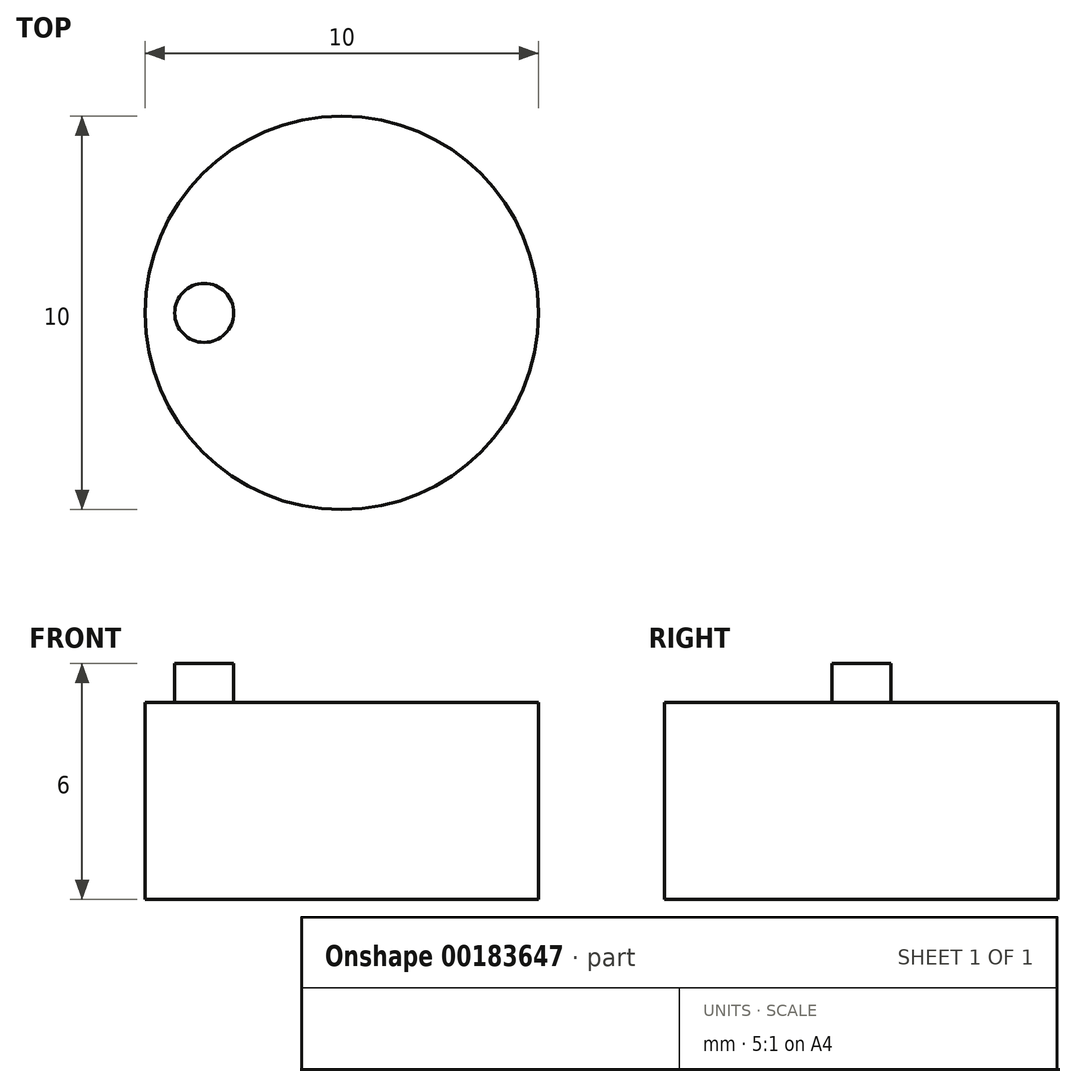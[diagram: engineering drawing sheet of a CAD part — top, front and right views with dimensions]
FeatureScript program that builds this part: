
annotation { "Feature Type Name" : "Feature", "Feature Type Description" : "" }
export const myFeature = defineFeature(function(context is Context, id is Id, definition is map)
    precondition{}
    {
        {
            var Q0;
            Q0=qCreatedBy(makeId("Top.planeOp"),FACE);
            var sketch = newSketch(context, id + "F0", { "sketchPlane" : qUnion([Q0])});
            skCircle(sketch, "E0", {"center": v(0, 0) * mm, "radius": 5 * mm});
            skLineSegment(sketch, "E1", {"start": v(-5, 0) * mm, "end": v(-3.5, 0) * mm});
            skPoint(sketch, "E2", {"position": v(-3.5, 0) * mm});
            skSolve(sketch);
        }
        {
            var Q0;
            Q0 = qSketchRegion(id + "F0", true);
            extrude(context, id + "F1", {"entities" : qUnion([Q0]), "depth" : 5 * mm});
        }
        {
            var Q0;
            Q0=makeQuery(id+"F1.opExtrude","CAP_FACE",FACE,{"disambiguationData":[OSD([sQuery(id+"F0.wireOp",EDGE,"E0")])],"isStart":false});
            var sketch = newSketch(context, id + "F2", { "sketchPlane" : qUnion([Q0])});
            skLineSegment(sketch, "E3", {"start": v(-5, 0) * mm, "end": v(-3.5, 0) * mm});
            skCircle(sketch, "E4", {"center": v(-3.5, 0) * mm, "radius": 0.75 * mm});
            skSolve(sketch);
        }
        {
            var Q0;
            Q0=makeQuery(id+"F2.imprint","IMPRINT",FACE,{"disambiguationData":[TD([[makeQuery(id+"F2.imprint","IMPRINT",EDGE,{"derivedFrom":sQuery(id+"F2.wireOp",EDGE,"E4")}),1.0]])]});
            extrude(context, id + "F3", {"entities" : qUnion([Q0]), "depth" : 1 * mm});
        }
    });
